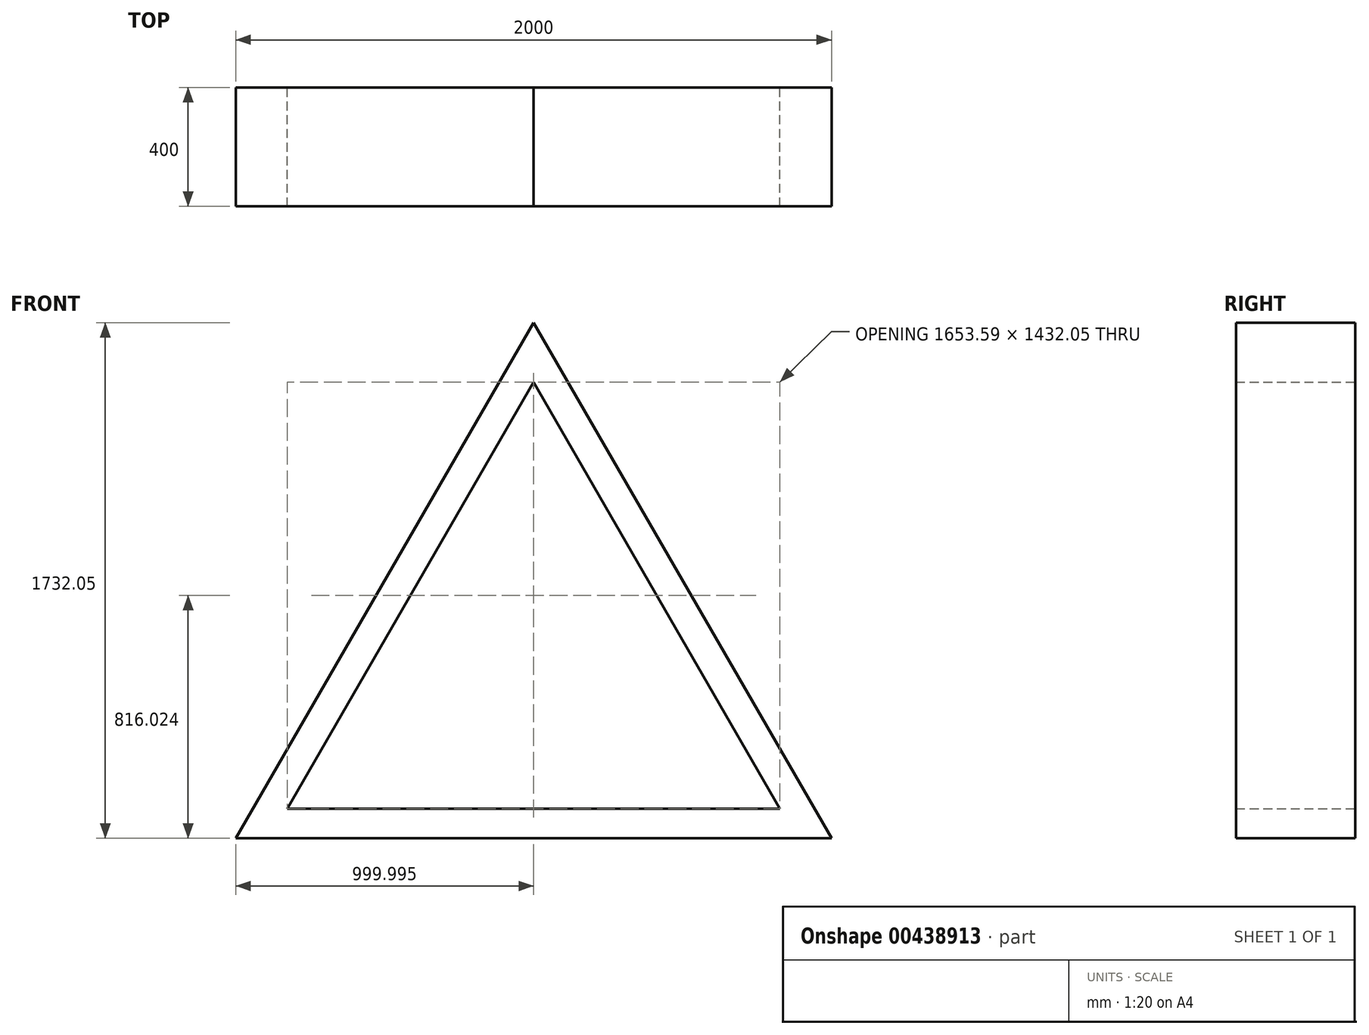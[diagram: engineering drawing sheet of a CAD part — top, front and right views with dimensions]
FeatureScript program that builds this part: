
annotation { "Feature Type Name" : "Feature", "Feature Type Description" : "" }
export const myFeature = defineFeature(function(context is Context, id is Id, definition is map)
    precondition{}
    {
        {
            var Q0;
            Q0=qCreatedBy(makeId("Front.planeOp"),FACE);
            var sketch = newSketch(context, id + "F0", { "sketchPlane" : qUnion([Q0])});
            skLineSegment(sketch, "E0", {"start": v(-272.77, -548.7) * mm, "end": v(1727.23, -548.7) * mm});
            skLineSegment(sketch, "E1", {"start": v(1727.23, -548.7) * mm, "end": v(727.23, 1183.35) * mm});
            skLineSegment(sketch, "E2", {"start": v(727.23, 1183.35) * mm, "end": v(-272.77, -548.7) * mm});
            skLineSegment(sketch, "E3.0", {"start": v(727.23, 983.35) * mm, "end": v(-99.57, -448.7) * mm});
            skLineSegment(sketch, "E3.1", {"start": v(1554.02, -448.7) * mm, "end": v(727.23, 983.35) * mm});
            skLineSegment(sketch, "E3.2", {"start": v(-99.57, -448.7) * mm, "end": v(1554.02, -448.7) * mm});
            skLineSegment(sketch, "E4", {"start": v(-99.57, -448.7) * mm, "end": v(-272.77, -548.7) * mm});
            skLineSegment(sketch, "E5", {"start": v(1554.02, -448.7) * mm, "end": v(1727.23, -548.7) * mm});
            skLineSegment(sketch, "E6", {"start": v(727.23, 1183.35) * mm, "end": v(727.23, 983.35) * mm});
            skSolve(sketch);
        }
        {
            var Q0;
            Q0 = qSketchRegion(id + "F0", true);
            extrude(context, id + "F1", {"entities" : qUnion([Q0]), "depth" : 400 * mm});
        }
    });
